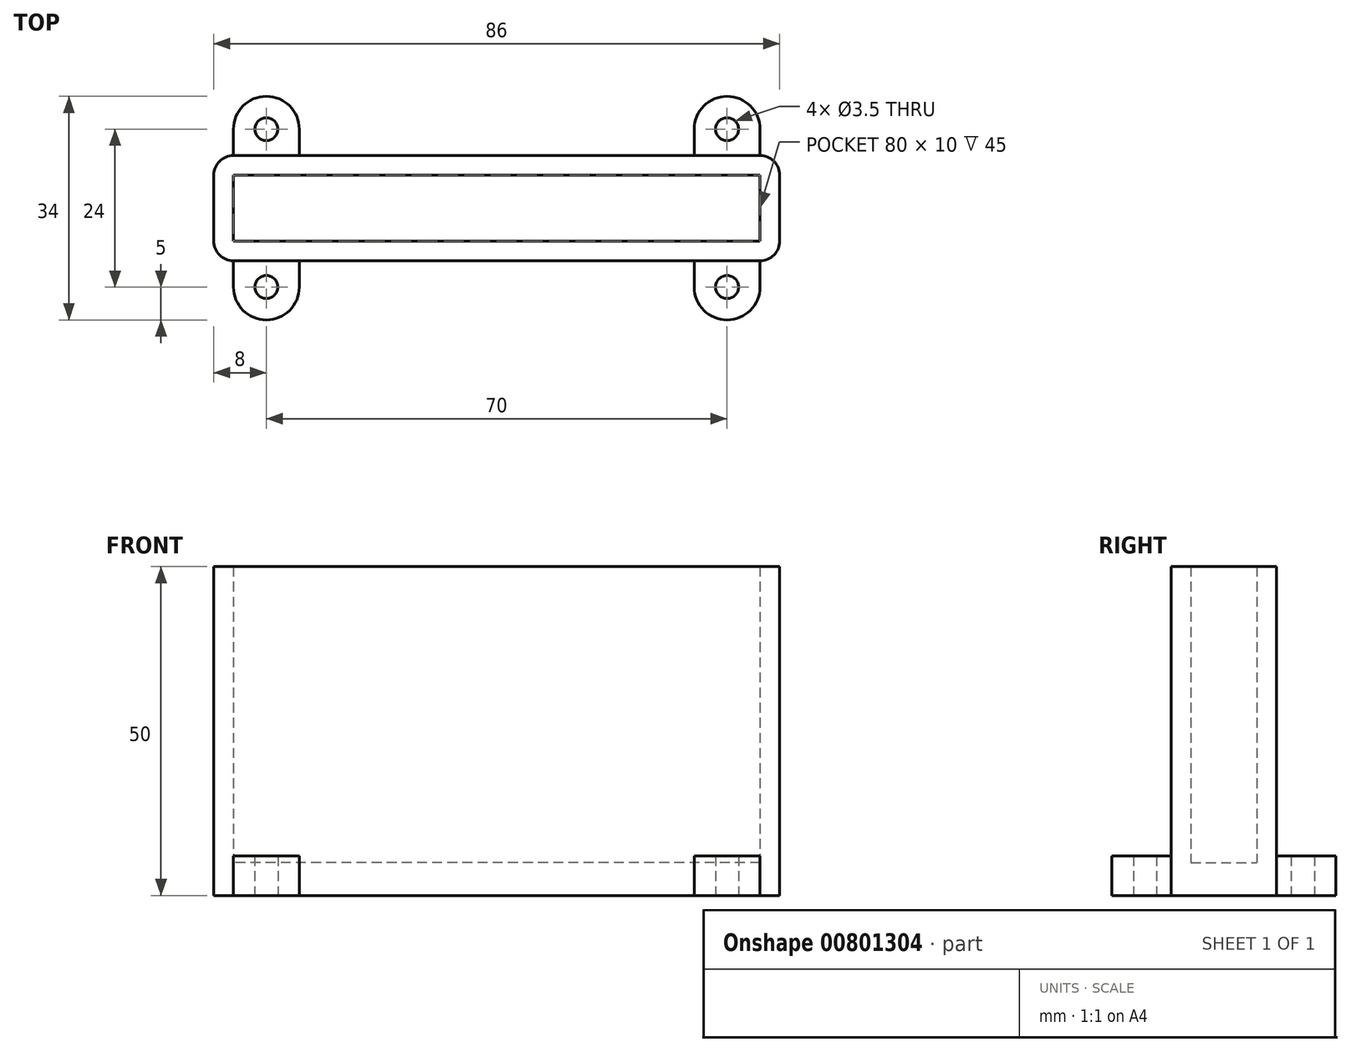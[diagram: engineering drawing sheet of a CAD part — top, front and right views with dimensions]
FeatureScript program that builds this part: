
annotation { "Feature Type Name" : "Feature", "Feature Type Description" : "" }
export const myFeature = defineFeature(function(context is Context, id is Id, definition is map)
    precondition{}
    {
        {
            var Q0;
            Q0=qCreatedBy(makeId("Top.planeOp"),FACE);
            var sketch = newSketch(context, id + "F0", { "sketchPlane" : qUnion([Q0])});
            skLineSegment(sketch, "E0.bottom", {"start": v(40, -5) * mm, "end": v(-40, -5) * mm});
            skLineSegment(sketch, "E0.top", {"start": v(40, 5) * mm, "end": v(-40, 5) * mm});
            skLineSegment(sketch, "E0.left", {"start": v(40, -5) * mm, "end": v(40, 5) * mm});
            skLineSegment(sketch, "E0.right", {"start": v(-40, -5) * mm, "end": v(-40, 5) * mm});
            skPoint(sketch, "E0.middle", {"position": v(0, 0) * mm});
            skLineSegment(sketch, "E1.0", {"start": v(40, 8) * mm, "end": v(-40, 8) * mm});
            skLineSegment(sketch, "E1.1", {"start": v(43, -5) * mm, "end": v(43, 5) * mm});
            skLineSegment(sketch, "E1.2", {"start": v(40, -8) * mm, "end": v(-40, -8) * mm});
            skLineSegment(sketch, "E1.3", {"start": v(-43, -5) * mm, "end": v(-43, 5) * mm});
            skPoint(sketch, "E2.visualSharp", {"position": v(-43, 8) * mm});
            skArc(sketch, "E2.filletArc", {"start": v(-40, 8) * mm, "mid": v(-42.12, 7.12) * mm, "end": v(-43, 5) * mm});
            skPoint(sketch, "E3.visualSharp", {"position": v(-43, -8) * mm});
            skArc(sketch, "E3.filletArc", {"start": v(-43, -5) * mm, "mid": v(-42.12, -7.12) * mm, "end": v(-40, -8) * mm});
            skPoint(sketch, "E4.visualSharp", {"position": v(43, 8) * mm});
            skArc(sketch, "E4.filletArc", {"start": v(43, 5) * mm, "mid": v(42.12, 7.12) * mm, "end": v(40, 8) * mm});
            skPoint(sketch, "E5.visualSharp", {"position": v(43, -8) * mm});
            skArc(sketch, "E5.filletArc", {"start": v(40, -8) * mm, "mid": v(42.12, -7.12) * mm, "end": v(43, -5) * mm});
            skLineSegment(sketch, "E6", {"start": v(40, -8) * mm, "end": v(40, -12) * mm});
            skLineSegment(sketch, "E7", {"start": v(-40, 8) * mm, "end": v(-40, 12) * mm});
            skLineSegment(sketch, "E8", {"start": v(-30, 12) * mm, "end": v(-40, 12) * mm});
            skLineSegment(sketch, "E9", {"start": v(-30, 12) * mm, "end": v(-30, 8) * mm});
            skLineSegment(sketch, "E10", {"start": v(40, 8) * mm, "end": v(40, 12) * mm});
            skLineSegment(sketch, "E11", {"start": v(40, 12) * mm, "end": v(30, 12) * mm});
            skLineSegment(sketch, "E12", {"start": v(30, 12) * mm, "end": v(30, 8) * mm});
            skArc(sketch, "E13", {"start": v(-30, 12) * mm, "mid": v(-35, 17) * mm, "end": v(-40, 12) * mm});
            skArc(sketch, "E14", {"start": v(40, 12) * mm, "mid": v(35, 17) * mm, "end": v(30, 12) * mm});
            skCircle(sketch, "E15", {"center": v(-35, 12) * mm, "radius": 1.75 * mm});
            skCircle(sketch, "E16", {"center": v(35, 12) * mm, "radius": 1.75 * mm});
            skLineSegment(sketch, "E17", {"start": v(40, -12) * mm, "end": v(30, -12) * mm});
            skLineSegment(sketch, "E18", {"start": v(30, -12) * mm, "end": v(30, -8) * mm});
            skLineSegment(sketch, "E19", {"start": v(-40, -8) * mm, "end": v(-40, -12) * mm});
            skLineSegment(sketch, "E20", {"start": v(-30, -12) * mm, "end": v(-40, -12) * mm});
            skLineSegment(sketch, "E21", {"start": v(-30, -12) * mm, "end": v(-30, -8) * mm});
            skArc(sketch, "E22", {"start": v(30, -12) * mm, "mid": v(35, -17) * mm, "end": v(40, -12) * mm});
            skArc(sketch, "E23", {"start": v(-40, -12) * mm, "mid": v(-35, -17) * mm, "end": v(-30, -12) * mm});
            skCircle(sketch, "E24", {"center": v(-35, -12) * mm, "radius": 1.75 * mm});
            skCircle(sketch, "E25", {"center": v(35, -12) * mm, "radius": 1.75 * mm});
            skSolve(sketch);
        }
        {
            var Q0;
            Q0=makeQuery(id+"F0.imprint","IMPRINT",FACE,{"disambiguationData":[TD([[makeQuery(id+"F0.imprint","IMPRINT",EDGE,{"derivedFrom":sQuery(id+"F0.wireOp",EDGE,"E0.bottom")}),1.0]])]});
            extrude(context, id + "F1", {"entities" : qUnion([Q0]), "depth" : 50 * mm, "offsetDistance" : 25 * mm});
        }
        {
            var Q0;
            Q0=qCreatedBy(makeId("Top.planeOp"),FACE);
            var sketch = newSketch(context, id + "F2", { "sketchPlane" : qUnion([Q0])});
            skLineSegment(sketch, "E26.bottom", {"start": v(40, -5) * mm, "end": v(-40, -5) * mm});
            skLineSegment(sketch, "E26.top", {"start": v(40, 5) * mm, "end": v(-40, 5) * mm});
            skLineSegment(sketch, "E26.left", {"start": v(40, -5) * mm, "end": v(40, 5) * mm});
            skLineSegment(sketch, "E26.right", {"start": v(-40, -5) * mm, "end": v(-40, 5) * mm});
            skPoint(sketch, "E26.middle", {"position": v(0, 0) * mm});
            skSolve(sketch);
        }
        {
            var Q0;
            Q0=makeQuery(id+"F2.imprint","IMPRINT",FACE,{"disambiguationData":[TD([[makeQuery(id+"F2.imprint","IMPRINT",EDGE,{"derivedFrom":sQuery(id+"F2.wireOp",EDGE,"E26.bottom")}),-1.0]])]});
            extrude(context, id + "F3", {"entities" : qUnion([Q0]), "operationType" : NewBodyOperationType.ADD, "depth" : 5 * mm, "offsetDistance" : 25 * mm});
        }
        {
            var Q0;
            Q0 = qSketchRegion(id + "F0", true);
            extrude(context, id + "F4", {"entities" : qUnion([Q0]), "operationType" : NewBodyOperationType.ADD, "depth" : 6 * mm, "offsetDistance" : 25 * mm});
        }
    });
